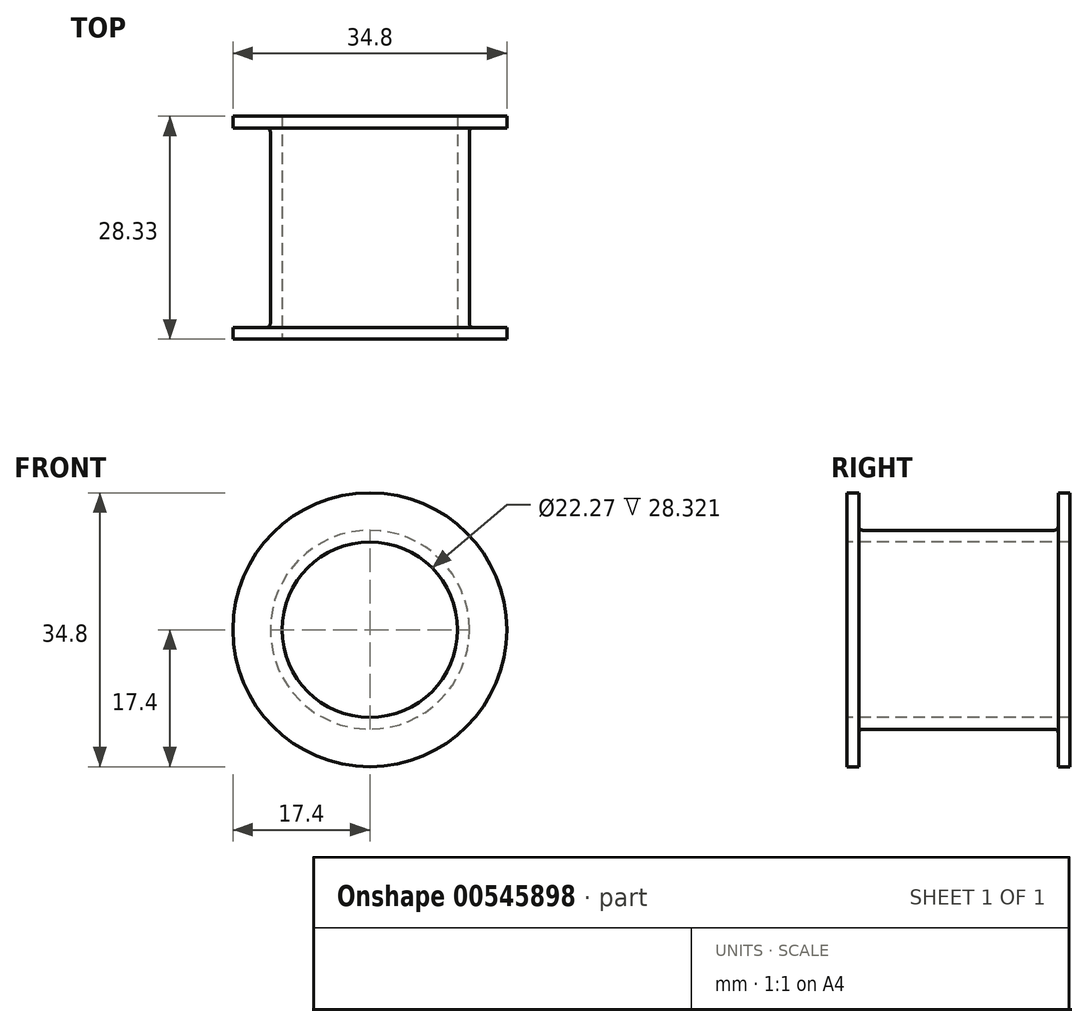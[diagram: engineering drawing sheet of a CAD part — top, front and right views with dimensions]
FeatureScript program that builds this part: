
annotation { "Feature Type Name" : "Feature", "Feature Type Description" : "" }
export const myFeature = defineFeature(function(context is Context, id is Id, definition is map)
    precondition{}
    {
        {
            var Q0;
            Q0=qCreatedBy(makeId("Top.planeOp"),FACE);
            var sketch = newSketch(context, id + "F0", { "sketchPlane" : qUnion([Q0])});
            skLineSegment(sketch, "E0", {"start": v(0, 0) * mm, "end": v(17.4, 0) * mm, "construction": true});
            skCircle(sketch, "E1", {"center": v(0, 0) * mm, "radius": 8.9 * mm, "construction": true});
            skLineSegment(sketch, "E2", {"start": v(17.4, 12.66) * mm, "end": v(13.14, 12.66) * mm});
            skLineSegment(sketch, "E3", {"start": v(17.4, -12.66) * mm, "end": v(13.14, -12.66) * mm});
            skLineSegment(sketch, "E4", {"start": v(0, -15.82) * mm, "end": v(0, 21.52) * mm, "construction": true});
            skLineSegment(sketch, "E5.0", {"start": v(17.4, -14.16) * mm, "end": v(11.14, -14.16) * mm});
            skLineSegment(sketch, "E5.2", {"start": v(17.4, 14.17) * mm, "end": v(11.14, 14.17) * mm});
            skLineSegment(sketch, "E6", {"start": v(17.4, 14.17) * mm, "end": v(17.4, 12.66) * mm});
            skLineSegment(sketch, "E7", {"start": v(17.4, -12.66) * mm, "end": v(17.4, -14.16) * mm});
            skLineSegment(sketch, "E8", {"start": v(11.14, 14.17) * mm, "end": v(11.14, -14.16) * mm});
            skLineSegment(sketch, "E9", {"start": v(12.64, 12.16) * mm, "end": v(12.64, -12.16) * mm});
            skPoint(sketch, "E10.visualSharp", {"position": v(12.64, 12.66) * mm});
            skArc(sketch, "E10.filletArc", {"start": v(13.14, 12.66) * mm, "mid": v(12.78, 12.52) * mm, "end": v(12.64, 12.16) * mm});
            skPoint(sketch, "E11.visualSharp", {"position": v(12.64, -12.66) * mm});
            skArc(sketch, "E11.filletArc", {"start": v(12.64, -12.16) * mm, "mid": v(12.78, -12.5) * mm, "end": v(13.14, -12.66) * mm});
            skPoint(sketch, "E12.visualSharp", {"position": v(11.14, 14.17) * mm});
            skPoint(sketch, "E13.visualSharp", {"position": v(11.14, -14.16) * mm});
            skSolve(sketch);
        }
        {
            var Q0;
            Q0=qSketchRegion(id+"F0",true);
            var Q1;
            Q1=sQuery(id+"F0.wireOp",EDGE,"E4");
            revolve(context, id + "F1", {"entities" : qUnion([Q0]), "axis" : qUnion([Q1]), "revolveType" : RevolveType.FULL});
        }
    });
